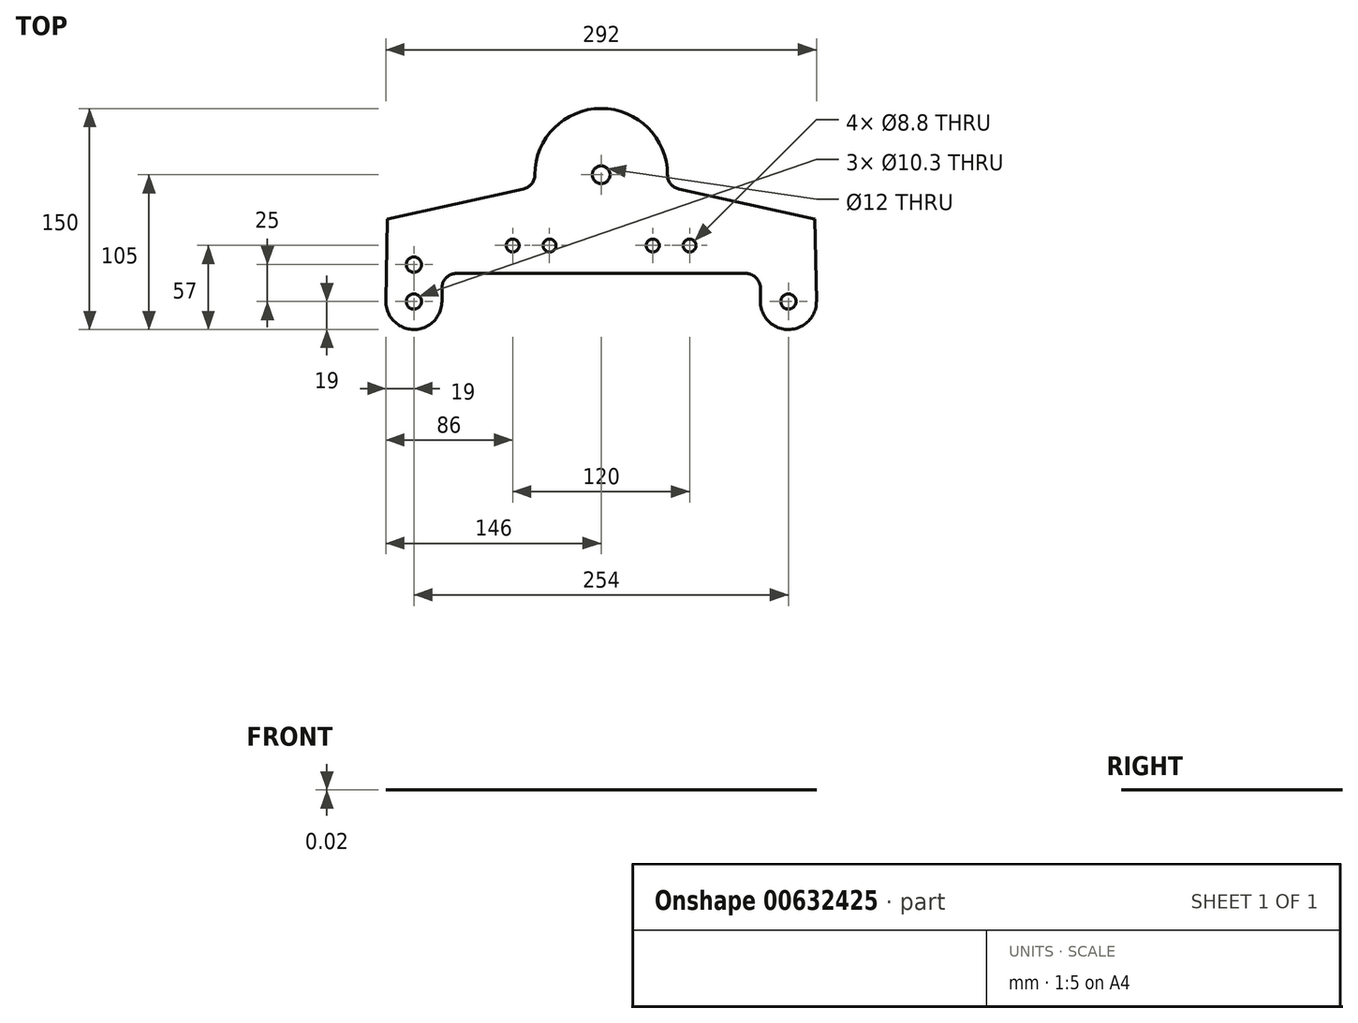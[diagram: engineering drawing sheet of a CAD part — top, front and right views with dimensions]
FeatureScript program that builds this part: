
annotation { "Feature Type Name" : "Feature", "Feature Type Description" : "" }
export const myFeature = defineFeature(function(context is Context, id is Id, definition is map)
    precondition{}
    {
        {
            var Q0;
            Q0=qCreatedBy(makeId("Front.planeOp"),FACE);
            var sketch = newSketch(context, id + "F0", { "sketchPlane" : qUnion([Q0])});
            skLineSegment(sketch, "E0", {"start": v(0, -64) * mm, "end": v(-107.95, -64) * mm, "construction": true});
            skArc(sketch, "E1", {"start": v(-97.61, -26.01) * mm, "mid": v(-104.93, -28.8) * mm, "end": v(-108, -36) * mm});
            skPoint(sketch, "E2", {"position": v(-127, -20) * mm});
            skPoint(sketch, "E3", {"position": v(-127, -45) * mm});
            skLineSegment(sketch, "E4", {"start": v(0, 86) * mm, "end": v(0, -265.9) * mm, "construction": true});
            skArc(sketch, "E5", {"start": v(0, 86) * mm, "mid": v(-31.82, 72.82) * mm, "end": v(-45, 41) * mm});
            skLineSegment(sketch, "E6", {"start": v(-97.61, -26.01) * mm, "end": v(0, -26.01) * mm});
            skArc(sketch, "E7", {"start": v(-146, -44.65) * mm, "mid": v(-127.18, -64) * mm, "end": v(-108, -45) * mm});
            skLineSegment(sketch, "E8", {"start": v(-108, -36) * mm, "end": v(-108, -45) * mm});
            skPoint(sketch, "E9", {"position": v(-60, -7) * mm});
            skPoint(sketch, "E10", {"position": v(-35, -7) * mm});
            skLineSegment(sketch, "E11", {"start": v(-145, 11) * mm, "end": v(-146, -44.65) * mm});
            skLineSegment(sketch, "E12", {"start": v(0, 86) * mm, "end": v(-181.62, 86) * mm, "construction": true});
            skArc(sketch, "E13", {"start": v(-52.86, 31.23) * mm, "mid": v(-47.2, 34.73) * mm, "end": v(-45, 41) * mm});
            skLineSegment(sketch, "E14", {"start": v(-145, 11) * mm, "end": v(-52.86, 31.23) * mm});
            skLineSegment(sketch, "E15.MirrorCS", {"start": v(97.61, -26.01) * mm, "end": v(0, -26.01) * mm});
            skArc(sketch, "E16.MirrorCS", {"start": v(97.61, -26.01) * mm, "mid": v(104.93, -28.8) * mm, "end": v(108, -36) * mm});
            skLineSegment(sketch, "E17.MirrorCS", {"start": v(108, -36) * mm, "end": v(108, -45) * mm});
            skArc(sketch, "E18.MirrorCS", {"start": v(146, -44.65) * mm, "mid": v(127.18, -64) * mm, "end": v(108, -45) * mm});
            skLineSegment(sketch, "E19.MirrorCS", {"start": v(145, 11) * mm, "end": v(146, -44.65) * mm});
            skLineSegment(sketch, "E20.MirrorCS", {"start": v(145, 11) * mm, "end": v(52.86, 31.23) * mm});
            skArc(sketch, "E21.MirrorCS", {"start": v(52.86, 31.23) * mm, "mid": v(47.2, 34.73) * mm, "end": v(45, 41) * mm});
            skArc(sketch, "E22.MirrorCS", {"start": v(0, 86) * mm, "mid": v(31.82, 72.82) * mm, "end": v(45, 41) * mm});
            skPoint(sketch, "E23.MirrorP", {"position": v(60, -7) * mm});
            skPoint(sketch, "E24.MirrorP", {"position": v(35, -7) * mm});
            skSolve(sketch);
        }
        {
            var Q0;
            Q0=makeQuery(id+"F0.imprint","IMPRINT",FACE,{"disambiguationData":[TD([[makeQuery(id+"F0.imprint","IMPRINT",EDGE,{"derivedFrom":sQuery(id+"F0.wireOp",EDGE,"E1")}),-1.0]])]});
            extrude(context, id + "F1", {"entities" : qUnion([Q0]), "oppositeDirection" : true, "depth" : 3 / 203.2 * mm, "offsetDistance" : 25 * mm});
        }
        {
            var Q0;
            Q0=sQuery(id+"F0.wireOp",VERTEX,"49026169-9cc1-4b2b-9f15-5b818d7ceaf6");
            var Q1;
            Q1=sQuery(id+"F0.wireOp",VERTEX,"E3");
            var Q2;
            Q2=sQuery(id+"F0.wireOp",VERTEX,"E2");
            var Q3;
            Q3=sQuery(id+"F0.wireOp",VERTEX,"E18.MirrorCS.center");
            var Q4;
            Q4=makeQuery(id+"F1.opExtrude","SWEPT_BODY",BODY,{"disambiguationData":[OSD([sQuery(id+"F0.wireOp",EDGE,"E1"),sQuery(id+"F0.wireOp",EDGE,"xtPmemIf-gyIq-8CIu-qO20-FqGxbV3oo2Kk"),sQuery(id+"F0.wireOp",EDGE,"s7WWwIfT-fBGv-45Z3-ybd3-wCjo1UOgPLNt"),sQuery(id+"F0.wireOp",EDGE,"E5"),sQuery(id+"F0.wireOp",EDGE,"E6"),sQuery(id+"F0.wireOp",EDGE,"E7"),sQuery(id+"F0.wireOp",EDGE,"E8"),sQuery(id+"F0.wireOp",EDGE,"260b5f50-7eb8-4c5e-be8f-84aa135686ed0.MirrorCS"),sQuery(id+"F0.wireOp",EDGE,"80b08b39-474e-4fc7-81a9-d6a70dbfd3950.MirrorCS"),sQuery(id+"F0.wireOp",EDGE,"9fdce0ba-6a57-4a2f-b5b0-556159f2299b0.MirrorCS"),sQuery(id+"F0.wireOp",EDGE,"48c13973-5ff3-466e-941a-d81f5d3f07270.MirrorCS"),sQuery(id+"F0.wireOp",EDGE,"E11"),sQuery(id+"F0.wireOp",EDGE,"7f56cd83-91ff-414f-9f72-f168bff41e8e0.MirrorCS"),sQuery(id+"F0.wireOp",EDGE,"d2a3d1a4-891f-4675-8b01-eafa5f5f5f100.MirrorCS"),sQuery(id+"F0.wireOp",EDGE,"7e9b2849-778b-4084-baa3-c97c17b6100d0.MirrorCS"),sQuery(id+"F0.wireOp",EDGE,"fde7ceaa-9184-4192-bcc4-d03bb320f3a80.MirrorCS")])]});
            hole(context, id + "F2", {"style" : HoleStyle.SIMPLE, "endStyle" : HoleEndStyle.THROUGH, "standardTappedOrClearance" : lookupTablePath({ "standard" : "ISO", "engagement" : "75%", "pitch" : "1.75 mm", "size" : "M12", "type" : "Tapped" }), "standardBlindInLast" : lookupTablePath({ "standard" : "ISO", "engagement" : "75%", "pitch" : "1.75 mm", "size" : "M12", "type" : "Tapped" }), "holeDiameter" : 10.3 * mm, "majorDiameter" : 12 * mm, "showTappedDepth" : true, "isTappedThrough" : true, "tappedDepth" : 12 * mm, "tapClearance" : 3, "startFromSketch" : true, "locations" : qUnion([Q0, Q1, Q2, Q3]), "scope" : qUnion([Q4])});
        }
        {
            var Q0;
            Q0=sQuery(id+"F0.wireOp",VERTEX,"E9");
            var Q1;
            Q1=sQuery(id+"F0.wireOp",VERTEX,"E10");
            var Q2;
            Q2=sQuery(id+"F0.wireOp",VERTEX,"99cd328e-8ba5-4b5a-8983-6f8a7f1e8098");
            var Q3;
            Q3=sQuery(id+"F0.wireOp",VERTEX,"5551c3a4-8f28-4cba-92c4-0bb35df48d52");
            var Q4;
            Q4=sQuery(id+"F0.wireOp",VERTEX,"E24.MirrorP");
            var Q5;
            Q5=sQuery(id+"F0.wireOp",VERTEX,"E23.MirrorP");
            var Q6;
            Q6=makeQuery(id+"F1.opExtrude","SWEPT_BODY",BODY,{"disambiguationData":[OSD([sQuery(id+"F0.wireOp",EDGE,"E1"),sQuery(id+"F0.wireOp",EDGE,"xtPmemIf-gyIq-8CIu-qO20-FqGxbV3oo2Kk"),sQuery(id+"F0.wireOp",EDGE,"s7WWwIfT-fBGv-45Z3-ybd3-wCjo1UOgPLNt"),sQuery(id+"F0.wireOp",EDGE,"E5"),sQuery(id+"F0.wireOp",EDGE,"E6"),sQuery(id+"F0.wireOp",EDGE,"E7"),sQuery(id+"F0.wireOp",EDGE,"E8"),sQuery(id+"F0.wireOp",EDGE,"260b5f50-7eb8-4c5e-be8f-84aa135686ed0.MirrorCS"),sQuery(id+"F0.wireOp",EDGE,"80b08b39-474e-4fc7-81a9-d6a70dbfd3950.MirrorCS"),sQuery(id+"F0.wireOp",EDGE,"9fdce0ba-6a57-4a2f-b5b0-556159f2299b0.MirrorCS"),sQuery(id+"F0.wireOp",EDGE,"48c13973-5ff3-466e-941a-d81f5d3f07270.MirrorCS"),sQuery(id+"F0.wireOp",EDGE,"E11"),sQuery(id+"F0.wireOp",EDGE,"7f56cd83-91ff-414f-9f72-f168bff41e8e0.MirrorCS"),sQuery(id+"F0.wireOp",EDGE,"d2a3d1a4-891f-4675-8b01-eafa5f5f5f100.MirrorCS"),sQuery(id+"F0.wireOp",EDGE,"7e9b2849-778b-4084-baa3-c97c17b6100d0.MirrorCS"),sQuery(id+"F0.wireOp",EDGE,"fde7ceaa-9184-4192-bcc4-d03bb320f3a80.MirrorCS")])]});
            hole(context, id + "F3", {"style" : HoleStyle.SIMPLE, "endStyle" : HoleEndStyle.THROUGH, "standardTappedOrClearance" : lookupTablePath({ "standard" : "ISO", "engagement" : "75%", "pitch" : "1.25 mm", "size" : "M10", "type" : "Tapped" }), "standardBlindInLast" : lookupTablePath({ "standard" : "ISO", "engagement" : "75%", "pitch" : "1.25 mm", "size" : "M10", "type" : "Tapped" }), "holeDiameter" : 8.8 * mm, "majorDiameter" : 10 * mm, "showTappedDepth" : true, "isTappedThrough" : true, "tappedDepth" : 12 * mm, "tapClearance" : 3, "startFromSketch" : true, "locations" : qUnion([Q0, Q1, Q2, Q3, Q4, Q5]), "scope" : qUnion([Q6])});
        }
        {
            var Q0;
            Q0=sQuery(id+"F0.wireOp",VERTEX,"260b5f50-7eb8-4c5e-be8f-84aa135686ed0.MirrorCS.center");
            var Q1;
            Q1=sQuery(id+"F0.wireOp",VERTEX,"E5.center");
            var Q2;
            Q2=makeQuery(id+"F1.opExtrude","SWEPT_BODY",BODY,{"disambiguationData":[OSD([sQuery(id+"F0.wireOp",EDGE,"E1"),sQuery(id+"F0.wireOp",EDGE,"xtPmemIf-gyIq-8CIu-qO20-FqGxbV3oo2Kk"),sQuery(id+"F0.wireOp",EDGE,"s7WWwIfT-fBGv-45Z3-ybd3-wCjo1UOgPLNt"),sQuery(id+"F0.wireOp",EDGE,"E5"),sQuery(id+"F0.wireOp",EDGE,"E6"),sQuery(id+"F0.wireOp",EDGE,"E7"),sQuery(id+"F0.wireOp",EDGE,"E8"),sQuery(id+"F0.wireOp",EDGE,"260b5f50-7eb8-4c5e-be8f-84aa135686ed0.MirrorCS"),sQuery(id+"F0.wireOp",EDGE,"80b08b39-474e-4fc7-81a9-d6a70dbfd3950.MirrorCS"),sQuery(id+"F0.wireOp",EDGE,"9fdce0ba-6a57-4a2f-b5b0-556159f2299b0.MirrorCS"),sQuery(id+"F0.wireOp",EDGE,"48c13973-5ff3-466e-941a-d81f5d3f07270.MirrorCS"),sQuery(id+"F0.wireOp",EDGE,"E11"),sQuery(id+"F0.wireOp",EDGE,"7f56cd83-91ff-414f-9f72-f168bff41e8e0.MirrorCS"),sQuery(id+"F0.wireOp",EDGE,"d2a3d1a4-891f-4675-8b01-eafa5f5f5f100.MirrorCS"),sQuery(id+"F0.wireOp",EDGE,"7e9b2849-778b-4084-baa3-c97c17b6100d0.MirrorCS"),sQuery(id+"F0.wireOp",EDGE,"fde7ceaa-9184-4192-bcc4-d03bb320f3a80.MirrorCS")])]});
            hole(context, id + "F4", {"style" : HoleStyle.SIMPLE, "endStyle" : HoleEndStyle.THROUGH, "standardTappedOrClearance" : lookupTablePath({ "standard" : "ISO", "size" : "12", "type" : "Drilled" }), "standardBlindInLast" : lookupTablePath({ "standard" : "ISO", "size" : "12", "type" : "Drilled" }), "holeDiameter" : 12 * mm, "majorDiameter" : 10 * mm, "isTappedThrough" : true, "tappedDepth" : 12 * mm, "tapClearance" : 3, "startFromSketch" : true, "locations" : qUnion([Q0, Q1]), "scope" : qUnion([Q2])});
        }
        {
            var Q0;
            Q0=makeQuery(id+"F1.opExtrude","SWEPT_BODY",BODY,{"disambiguationData":[OSD([sQuery(id+"F0.wireOp",EDGE,"E1"),sQuery(id+"F0.wireOp",EDGE,"xtPmemIf-gyIq-8CIu-qO20-FqGxbV3oo2Kk"),sQuery(id+"F0.wireOp",EDGE,"s7WWwIfT-fBGv-45Z3-ybd3-wCjo1UOgPLNt"),sQuery(id+"F0.wireOp",EDGE,"E5"),sQuery(id+"F0.wireOp",EDGE,"E6"),sQuery(id+"F0.wireOp",EDGE,"E7"),sQuery(id+"F0.wireOp",EDGE,"E8"),sQuery(id+"F0.wireOp",EDGE,"260b5f50-7eb8-4c5e-be8f-84aa135686ed0.MirrorCS"),sQuery(id+"F0.wireOp",EDGE,"80b08b39-474e-4fc7-81a9-d6a70dbfd3950.MirrorCS"),sQuery(id+"F0.wireOp",EDGE,"9fdce0ba-6a57-4a2f-b5b0-556159f2299b0.MirrorCS"),sQuery(id+"F0.wireOp",EDGE,"48c13973-5ff3-466e-941a-d81f5d3f07270.MirrorCS"),sQuery(id+"F0.wireOp",EDGE,"E11"),sQuery(id+"F0.wireOp",EDGE,"7f56cd83-91ff-414f-9f72-f168bff41e8e0.MirrorCS"),sQuery(id+"F0.wireOp",EDGE,"d2a3d1a4-891f-4675-8b01-eafa5f5f5f100.MirrorCS"),sQuery(id+"F0.wireOp",EDGE,"7e9b2849-778b-4084-baa3-c97c17b6100d0.MirrorCS"),sQuery(id+"F0.wireOp",EDGE,"fde7ceaa-9184-4192-bcc4-d03bb320f3a80.MirrorCS")])]});
            var Q1;
            Q1=sQuery(id+"F0.wireOp",EDGE,"E0");
            transform(context, id + "F5", {"entities" : qUnion([Q0]), "transformType" : TransformType.ROTATION, "transformAxis" : qUnion([Q1]), "angle" : 90 * degree, "makeCopy" : false});
        }
    });
